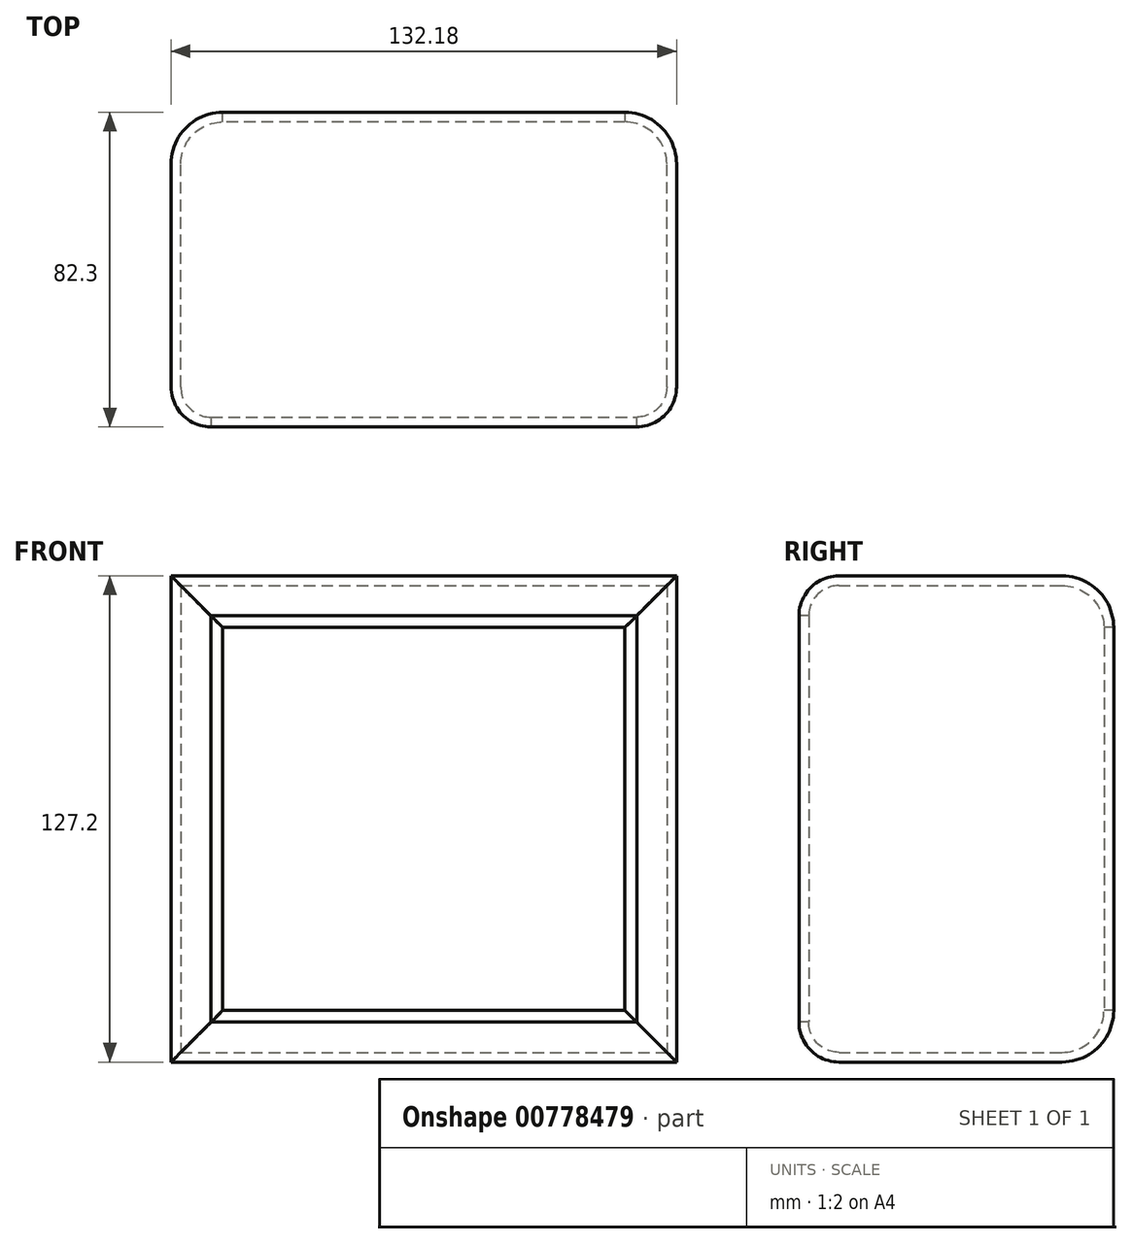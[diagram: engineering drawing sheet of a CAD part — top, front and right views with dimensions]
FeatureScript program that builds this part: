
annotation { "Feature Type Name" : "Feature", "Feature Type Description" : "" }
export const myFeature = defineFeature(function(context is Context, id is Id, definition is map)
    precondition{}
    {
        {
            var Q0;
            Q0=qCreatedBy(makeId("Front.planeOp"),FACE);
            var sketch = newSketch(context, id + "F0", { "sketchPlane" : qUnion([Q0])});
            skLineSegment(sketch, "E0.bottom", {"start": v(-63.16, 61.4) * mm, "end": v(69.02, 61.4) * mm});
            skLineSegment(sketch, "E0.top", {"start": v(-63.16, -65.8) * mm, "end": v(69.02, -65.8) * mm});
            skLineSegment(sketch, "E0.left", {"start": v(-63.16, 61.4) * mm, "end": v(-63.16, -65.8) * mm});
            skLineSegment(sketch, "E0.right", {"start": v(69.02, 61.4) * mm, "end": v(69.02, -65.8) * mm});
            skSolve(sketch);
        }
        {
            var Q0;
            Q0=makeQuery(id+"F0.imprint","IMPRINT",FACE,{"disambiguationData":[TD([[makeQuery(id+"F0.imprint","IMPRINT",EDGE,{"derivedFrom":sQuery(id+"F0.wireOp",EDGE,"E0.bottom")}),-1.0]])]});
            extrude(context, id + "F1", {"entities" : qUnion([Q0]), "depth" : 82.3 * mm, "offsetDistance" : 25.4 * mm});
        }
        {
            var Q0;
            Q0=makeQuery(id+"F1.opExtrude","CAP_FACE",FACE,{"disambiguationData":[OSD([sQuery(id+"F0.wireOp",EDGE,"E0.bottom"),sQuery(id+"F0.wireOp",EDGE,"E0.top"),sQuery(id+"F0.wireOp",EDGE,"E0.left"),sQuery(id+"F0.wireOp",EDGE,"E0.right")])],"isStart":false});
            fillet(context, id + "F2", {"entities" : qUnion([Q0]), "radius" : 10.42 * mm, "tangentPropagation" : true, "allowEdgeOverflow" : false});
        }
        {
            var Q0;
            Q0=makeQuery(id+"F1.opExtrude","CAP_FACE",FACE,{"disambiguationData":[OSD([sQuery(id+"F0.wireOp",EDGE,"E0.bottom"),sQuery(id+"F0.wireOp",EDGE,"E0.top"),sQuery(id+"F0.wireOp",EDGE,"E0.left"),sQuery(id+"F0.wireOp",EDGE,"E0.right")])],"isStart":true});
            fillet(context, id + "F3", {"entities" : qUnion([Q0]), "radius" : 13.5 * mm, "tangentPropagation" : true, "allowEdgeOverflow" : false});
        }
        {
            var Q0;
            Q0=makeQuery(id+"F1.opExtrude","CAP_FACE",FACE,{"disambiguationData":[OSD([sQuery(id+"F0.wireOp",EDGE,"E0.bottom"),sQuery(id+"F0.wireOp",EDGE,"E0.top"),sQuery(id+"F0.wireOp",EDGE,"E0.left"),sQuery(id+"F0.wireOp",EDGE,"E0.right")])],"isStart":false});
            var Q1;
            Q1=makeQuery(id+"F1.opExtrude","CAP_FACE",FACE,{"disambiguationData":[OSD([sQuery(id+"F0.wireOp",EDGE,"E0.bottom"),sQuery(id+"F0.wireOp",EDGE,"E0.top"),sQuery(id+"F0.wireOp",EDGE,"E0.left"),sQuery(id+"F0.wireOp",EDGE,"E0.right")])],"isStart":true});
            shell(context, id + "F4", {"entities" : qUnion([Q0, Q1]), "thickness" : 2.54 * mm});
        }
    });
